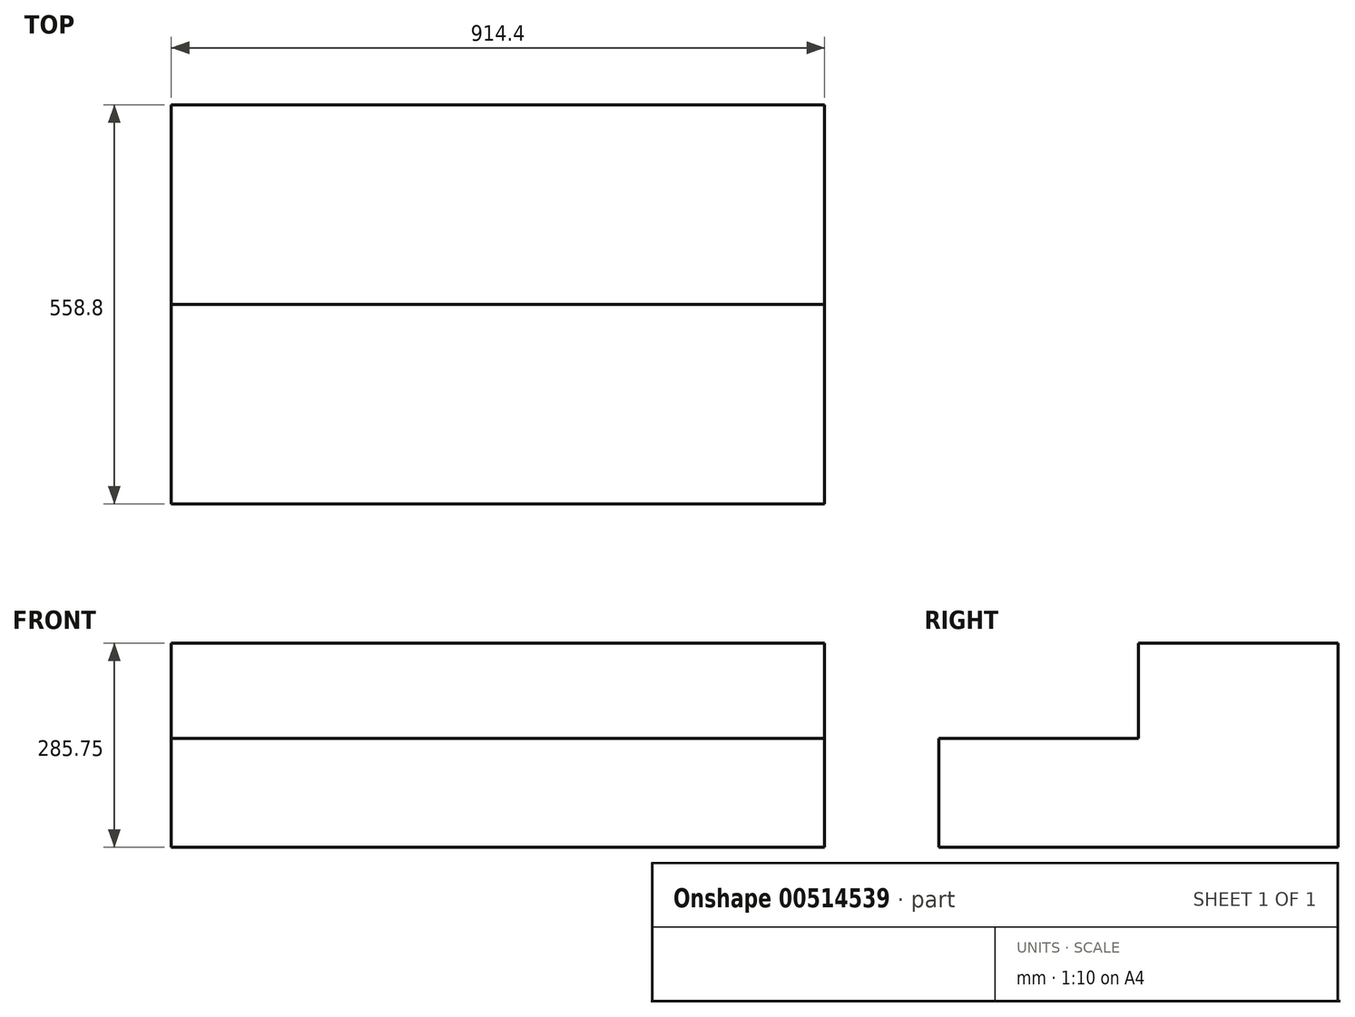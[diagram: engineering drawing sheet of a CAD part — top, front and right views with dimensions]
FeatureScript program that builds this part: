
annotation { "Feature Type Name" : "Feature", "Feature Type Description" : "" }
export const myFeature = defineFeature(function(context is Context, id is Id, definition is map)
    precondition{}
    {
        {
            var Q0;
            Q0=qCreatedBy(makeId("Top.planeOp"),FACE);
            var sketch = newSketch(context, id + "F0", { "sketchPlane" : qUnion([Q0])});
            skLineSegment(sketch, "E0.bottom", {"start": v(457.2, 279.4) * mm, "end": v(-457.2, 279.4) * mm});
            skLineSegment(sketch, "E0.top", {"start": v(457.2, -279.4) * mm, "end": v(-457.2, -279.4) * mm});
            skLineSegment(sketch, "E0.left", {"start": v(457.2, 279.4) * mm, "end": v(457.2, -279.4) * mm});
            skLineSegment(sketch, "E0.right", {"start": v(-457.2, 279.4) * mm, "end": v(-457.2, -279.4) * mm});
            skPoint(sketch, "E0.middle", {"position": v(0, 0) * mm});
            skSolve(sketch);
        }
        {
            var Q0;
            Q0=makeQuery(id+"F0.imprint","IMPRINT",FACE,{"disambiguationData":[TD([[makeQuery(id+"F0.imprint","IMPRINT",EDGE,{"derivedFrom":sQuery(id+"F0.wireOp",EDGE,"E0.bottom")}),1.0]])]});
            extrude(context, id + "F1", {"entities" : qUnion([Q0]), "depth" : 152.4 * mm, "offsetDistance" : 25.4 * mm});
        }
        {
            var Q0;
            Q0=makeQuery(id+"F1.opExtrude","CAP_FACE",FACE,{"disambiguationData":[OSD([sQuery(id+"F0.wireOp",EDGE,"E0.bottom"),sQuery(id+"F0.wireOp",EDGE,"E0.top"),sQuery(id+"F0.wireOp",EDGE,"E0.left"),sQuery(id+"F0.wireOp",EDGE,"E0.right")])],"isStart":false});
            var sketch = newSketch(context, id + "F2", { "sketchPlane" : qUnion([Q0])});
            skLineSegment(sketch, "E1.bottom", {"start": v(-457.2, 279.4) * mm, "end": v(457.2, 279.4) * mm});
            skLineSegment(sketch, "E1.top", {"start": v(-457.2, 0) * mm, "end": v(457.2, 0) * mm});
            skLineSegment(sketch, "E1.left", {"start": v(-457.2, 279.4) * mm, "end": v(-457.2, 0) * mm});
            skLineSegment(sketch, "E1.right", {"start": v(457.2, 279.4) * mm, "end": v(457.2, 0) * mm});
            skSolve(sketch);
        }
        {
            var Q0;
            Q0=makeQuery(id+"F2.imprint","IMPRINT",FACE,{"disambiguationData":[TD([[makeQuery(id+"F2.imprint","IMPRINT",EDGE,{"derivedFrom":sQuery(id+"F2.wireOp",EDGE,"E1.bottom")}),1.0]])]});
            extrude(context, id + "F3", {"entities" : qUnion([Q0]), "operationType" : NewBodyOperationType.ADD, "depth" : 133.35 * mm, "offsetDistance" : 25.4 * mm});
        }
    });
